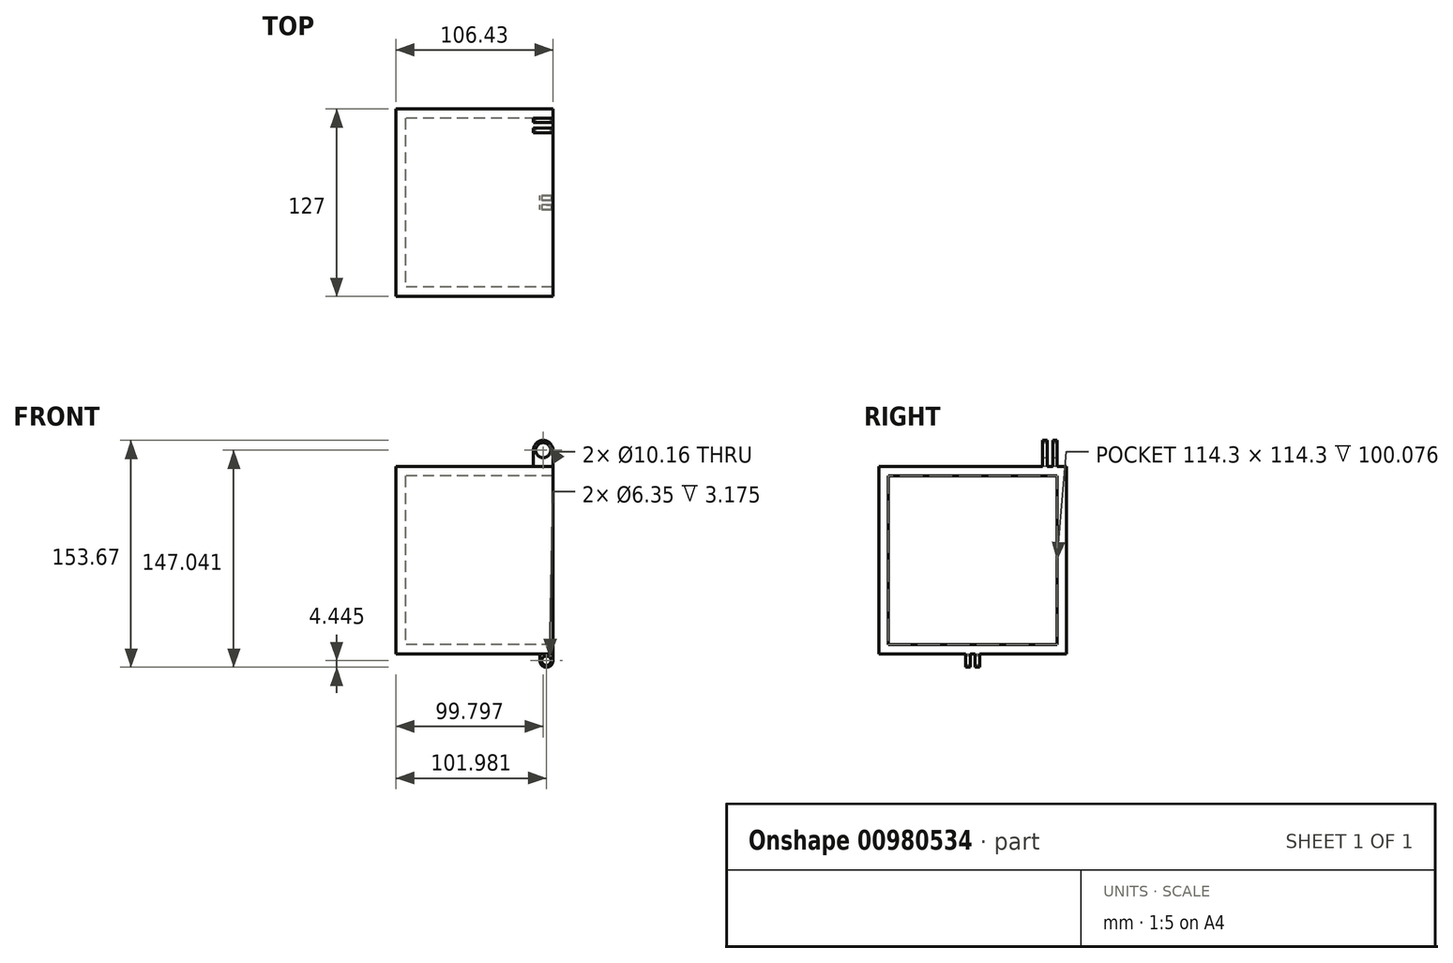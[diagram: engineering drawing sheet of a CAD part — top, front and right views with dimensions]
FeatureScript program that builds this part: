
annotation { "Feature Type Name" : "Feature", "Feature Type Description" : "" }
export const myFeature = defineFeature(function(context is Context, id is Id, definition is map)
    precondition{}
    {
        {
            var Q0;
            Q0=qCreatedBy(makeId("Right.planeOp"),FACE);
            var sketch = newSketch(context, id + "F0", { "sketchPlane" : qUnion([Q0])});
            skLineSegment(sketch, "E0.bottom", {"start": v(63.5, 63.5) * mm, "end": v(-63.5, 63.5) * mm});
            skLineSegment(sketch, "E0.top", {"start": v(63.5, -63.5) * mm, "end": v(-63.5, -63.5) * mm});
            skLineSegment(sketch, "E0.left", {"start": v(63.5, 63.5) * mm, "end": v(63.5, -63.5) * mm});
            skLineSegment(sketch, "E0.right", {"start": v(-63.5, 63.5) * mm, "end": v(-63.5, -63.5) * mm});
            skPoint(sketch, "E0.middle", {"position": v(0, 0) * mm});
            skLineSegment(sketch, "E1.bottom", {"start": v(57.15, 57.15) * mm, "end": v(-57.15, 57.15) * mm});
            skLineSegment(sketch, "E1.top", {"start": v(57.15, -57.15) * mm, "end": v(-57.15, -57.15) * mm});
            skLineSegment(sketch, "E1.left", {"start": v(57.15, 57.15) * mm, "end": v(57.15, -57.15) * mm});
            skLineSegment(sketch, "E1.right", {"start": v(-57.15, 57.15) * mm, "end": v(-57.15, -57.15) * mm});
            skSolve(sketch);
        }
        {
            var Q0;
            Q0 = qSketchRegion(id + "F0", true);
            var Q1;
            Q1=makeQuery(id+"F0.imprint","IMPRINT",FACE,{"disambiguationData":[TD([[makeQuery(id+"F0.imprint","IMPRINT",EDGE,{"derivedFrom":sQuery(id+"F0.wireOp",EDGE,"E0.bottom")}),1.0]])]});
            extrude(context, id + "F1", {"entities" : qUnion([Q0, Q1]), "depth" : 106.43 * mm, "offsetDistance" : 25.4 * mm});
        }
        {
            var Q0;
            Q0=qCreatedBy(makeId("Right.planeOp"),FACE);
            var sketch = newSketch(context, id + "F2", { "sketchPlane" : qUnion([Q0])});
            skLineSegment(sketch, "E2.bottom", {"start": v(-63.5, 63.5) * mm, "end": v(63.5, 63.5) * mm});
            skLineSegment(sketch, "E2.top", {"start": v(-63.5, -63.5) * mm, "end": v(63.5, -63.5) * mm});
            skLineSegment(sketch, "E2.left", {"start": v(-63.5, 63.5) * mm, "end": v(-63.5, -63.5) * mm});
            skLineSegment(sketch, "E2.right", {"start": v(63.5, 63.5) * mm, "end": v(63.5, -63.5) * mm});
            skSolve(sketch);
        }
        {
            var Q0;
            Q0 = qSketchRegion(id + "F2", true);
            extrude(context, id + "F3", {"entities" : qUnion([Q0]), "operationType" : NewBodyOperationType.ADD, "depth" : 6.35 * mm, "offsetDistance" : 25.4 * mm});
        }
        {
            var Q0;
            Q0=makeQuery(id+"F1.opExtrude","SWEPT_FACE",FACE,{"disambiguationData":[OSD([sQuery(id+"F0.wireOp",EDGE,"E0.bottom")])]});
            var sketch = newSketch(context, id + "F4", { "sketchPlane" : qUnion([Q0])});
            skLineSegment(sketch, "E3.bottom", {"start": v(106.43, 57.15) * mm, "end": v(93.17, 57.15) * mm});
            skLineSegment(sketch, "E3.top", {"start": v(106.43, 47.5) * mm, "end": v(93.17, 47.5) * mm});
            skLineSegment(sketch, "E3.left", {"start": v(106.43, 57.15) * mm, "end": v(106.43, 47.5) * mm});
            skLineSegment(sketch, "E3.right", {"start": v(93.17, 57.15) * mm, "end": v(93.17, 47.5) * mm});
            skSolve(sketch);
        }
        {
            var Q0;
            Q0=makeQuery(id+"F4.imprint","IMPRINT",FACE,{"disambiguationData":[TD([[makeQuery(id+"F4.imprint","IMPRINT",EDGE,{"derivedFrom":sQuery(id+"F4.wireOp",EDGE,"E3.bottom")}),1.0]])]});
            extrude(context, id + "F5", {"entities" : qUnion([Q0]), "operationType" : NewBodyOperationType.ADD, "depth" : 17.78 * mm, "offsetDistance" : 25.4 * mm});
        }
        {
            var Q0;
            Q0=makeQuery(id+"F5.boolean.opBoolean","MERGE",FACE,{"derivedFrom":[makeQuery(id+"F1.opExtrude","CAP_FACE",FACE,{"disambiguationData":[OSD([sQuery(id+"F0.wireOp",EDGE,"E0.bottom"),sQuery(id+"F0.wireOp",EDGE,"E0.top"),sQuery(id+"F0.wireOp",EDGE,"E0.left"),sQuery(id+"F0.wireOp",EDGE,"E0.right"),sQuery(id+"F0.wireOp",EDGE,"E1.bottom"),sQuery(id+"F0.wireOp",EDGE,"E1.top"),sQuery(id+"F0.wireOp",EDGE,"E1.left"),sQuery(id+"F0.wireOp",EDGE,"E1.right")])],"isStart":false}),makeQuery(id+"F5.opExtrude","SWEPT_FACE",FACE,{"disambiguationData":[OSD([sQuery(id+"F4.wireOp",EDGE,"E3.left")])]})]});
            var sketch = newSketch(context, id + "F6", { "sketchPlane" : qUnion([Q0])});
            skLineSegment(sketch, "E4.bottom", {"start": v(54.23, 81.28) * mm, "end": v(50.42, 81.28) * mm});
            skLineSegment(sketch, "E4.top", {"start": v(54.23, 63.5) * mm, "end": v(50.42, 63.5) * mm});
            skLineSegment(sketch, "E4.left", {"start": v(54.23, 81.28) * mm, "end": v(54.23, 63.5) * mm});
            skLineSegment(sketch, "E4.right", {"start": v(50.42, 81.28) * mm, "end": v(50.42, 63.5) * mm});
            skSolve(sketch);
        }
        {
            var Q0;
            Q0 = qSketchRegion(id + "F6", true);
            extrude(context, id + "F7", {"entities" : qUnion([Q0]), "operationType" : NewBodyOperationType.REMOVE, "endBound" : BoundingType.THROUGH_ALL, "oppositeDirection" : true, "depth" : 25.4 * mm, "offsetDistance" : 25.4 * mm});
        }
        {
            var Q0;
            {var subQ0=sQuery(id+"F4.wireOp",EDGE,"E3.left");var subQ1=sQuery(id+"F4.wireOp",EDGE,"E3.bottom");Q0=makeQuery(id+"F7.boolean.opBoolean","SPLIT",EDGE,{"disambiguationData":[TD([makeQuery(id+"F5.opExtrude","SWEPT_FACE",FACE,{"disambiguationData":[OSD([subQ1])]})])],"derivedFrom":makeQuery(id+"F5.opExtrude","CAP_EDGE",EDGE,{"disambiguationData":[OSD([subQ0])],"isStart":false})});}
            var Q1;
            {var subQ0=sQuery(id+"F4.wireOp",EDGE,"E3.left");var subQ1=sQuery(id+"F4.wireOp",EDGE,"E3.top");Q1=makeQuery(id+"F7.boolean.opBoolean","SPLIT",EDGE,{"disambiguationData":[TD([makeQuery(id+"F5.opExtrude","SWEPT_FACE",FACE,{"disambiguationData":[OSD([subQ1])]})])],"derivedFrom":makeQuery(id+"F5.opExtrude","CAP_EDGE",EDGE,{"disambiguationData":[OSD([subQ0])],"isStart":false})});}
            var Q2;
            {var subQ0=sQuery(id+"F4.wireOp",EDGE,"E3.bottom");var subQ1=sQuery(id+"F4.wireOp",EDGE,"E3.right");Q2=makeQuery(id+"F7.boolean.opBoolean","SPLIT",EDGE,{"disambiguationData":[TD([makeQuery(id+"F5.opExtrude","SWEPT_FACE",FACE,{"disambiguationData":[OSD([subQ0])]})])],"derivedFrom":makeQuery(id+"F5.opExtrude","CAP_EDGE",EDGE,{"disambiguationData":[OSD([subQ1])],"isStart":false})});}
            var Q3;
            {var subQ0=sQuery(id+"F4.wireOp",EDGE,"E3.right");var subQ1=sQuery(id+"F4.wireOp",EDGE,"E3.top");Q3=makeQuery(id+"F7.boolean.opBoolean","SPLIT",EDGE,{"disambiguationData":[TD([makeQuery(id+"F5.opExtrude","SWEPT_FACE",FACE,{"disambiguationData":[OSD([subQ1])]})])],"derivedFrom":makeQuery(id+"F5.opExtrude","CAP_EDGE",EDGE,{"disambiguationData":[OSD([subQ0])],"isStart":false})});}
            fillet(context, id + "F8", {"entities" : qUnion([Q0, Q1, Q2, Q3]), "radius" : 6.63 * mm, "tangentPropagation" : true, "allowEdgeOverflow" : false});
        }
        {
            var Q0;
            Q0=makeQuery(id+"F5.opExtrude","SWEPT_FACE",FACE,{"disambiguationData":[OSD([sQuery(id+"F4.wireOp",EDGE,"E3.bottom")])]});
            var sketch = newSketch(context, id + "F9", { "sketchPlane" : qUnion([Q0])});
            skCircle(sketch, "E5", {"center": v(-99.8, 74.65) * mm, "radius": 5.08 * mm});
            skSolve(sketch);
        }
        {
            var Q0;
            Q0 = qSketchRegion(id + "F9", true);
            extrude(context, id + "F10", {"entities" : qUnion([Q0]), "operationType" : NewBodyOperationType.REMOVE, "oppositeDirection" : true, "depth" : 25.4 * mm, "offsetDistance" : 25.4 * mm});
        }
        {
            var Q0;
            Q0=makeQuery(id+"F1.opExtrude","SWEPT_FACE",FACE,{"disambiguationData":[OSD([sQuery(id+"F0.wireOp",EDGE,"E0.top")])]});
            var sketch = newSketch(context, id + "F11", { "sketchPlane" : qUnion([Q0])});
            skLineSegment(sketch, "E6.bottom", {"start": v(106.43, 4.83) * mm, "end": v(97.54, 4.83) * mm});
            skLineSegment(sketch, "E6.top", {"start": v(106.43, 1.65) * mm, "end": v(97.54, 1.65) * mm});
            skLineSegment(sketch, "E6.left", {"start": v(106.43, 4.83) * mm, "end": v(106.43, 1.65) * mm});
            skLineSegment(sketch, "E6.right", {"start": v(97.54, 4.83) * mm, "end": v(97.54, 1.65) * mm});
            skLineSegment(sketch, "E7.bottom", {"start": v(106.43, -1.65) * mm, "end": v(97.54, -1.65) * mm});
            skLineSegment(sketch, "E7.top", {"start": v(106.43, -4.83) * mm, "end": v(97.54, -4.83) * mm});
            skLineSegment(sketch, "E7.left", {"start": v(106.43, -1.65) * mm, "end": v(106.43, -4.83) * mm});
            skLineSegment(sketch, "E7.right", {"start": v(97.54, -1.65) * mm, "end": v(97.54, -4.83) * mm});
            skLineSegment(sketch, "E8", {"start": v(106.43, 0) * mm, "end": v(106.43, -1.65) * mm, "construction": true});
            skLineSegment(sketch, "E9", {"start": v(106.43, 0) * mm, "end": v(106.43, 1.65) * mm, "construction": true});
            skSolve(sketch);
        }
        {
            var Q0;
            Q0 = qSketchRegion(id + "F11", true);
            extrude(context, id + "F12", {"entities" : qUnion([Q0]), "operationType" : NewBodyOperationType.ADD, "depth" : 8.9 * mm, "offsetDistance" : 25.4 * mm});
        }
        {
            var Q0;
            Q0=makeQuery(id+"F12.opExtrude","CAP_EDGE",EDGE,{"disambiguationData":[OSD([sQuery(id+"F11.wireOp",EDGE,"E6.right")])],"isStart":false});
            var Q1;
            Q1=makeQuery(id+"F12.opExtrude","CAP_EDGE",EDGE,{"disambiguationData":[OSD([sQuery(id+"F11.wireOp",EDGE,"E7.right")])],"isStart":false});
            var Q2;
            Q2=makeQuery(id+"F12.opExtrude","CAP_EDGE",EDGE,{"disambiguationData":[OSD([sQuery(id+"F11.wireOp",EDGE,"E7.left")])],"isStart":false});
            var Q3;
            Q3=makeQuery(id+"F12.opExtrude","CAP_EDGE",EDGE,{"disambiguationData":[OSD([sQuery(id+"F11.wireOp",EDGE,"E6.left")])],"isStart":false});
            fillet(context, id + "F13", {"entities" : qUnion([Q0, Q1, Q2, Q3]), "radius" : 4.44 * mm, "tangentPropagation" : true, "allowEdgeOverflow" : false});
        }
        {
            var Q0;
            Q0=makeQuery(id+"F12.opExtrude","SWEPT_FACE",FACE,{"disambiguationData":[OSD([sQuery(id+"F11.wireOp",EDGE,"E6.bottom")])]});
            var sketch = newSketch(context, id + "F14", { "sketchPlane" : qUnion([Q0])});
            skCircle(sketch, "E10", {"center": v(101.98, -67.94) * mm, "radius": 3.17 * mm});
            skSolve(sketch);
        }
        {
            var Q0;
            Q0 = qSketchRegion(id + "F14", true);
            extrude(context, id + "F15", {"entities" : qUnion([Q0]), "operationType" : NewBodyOperationType.REMOVE, "oppositeDirection" : true, "depth" : 25.4 * mm, "offsetDistance" : 25.4 * mm});
        }
    });
